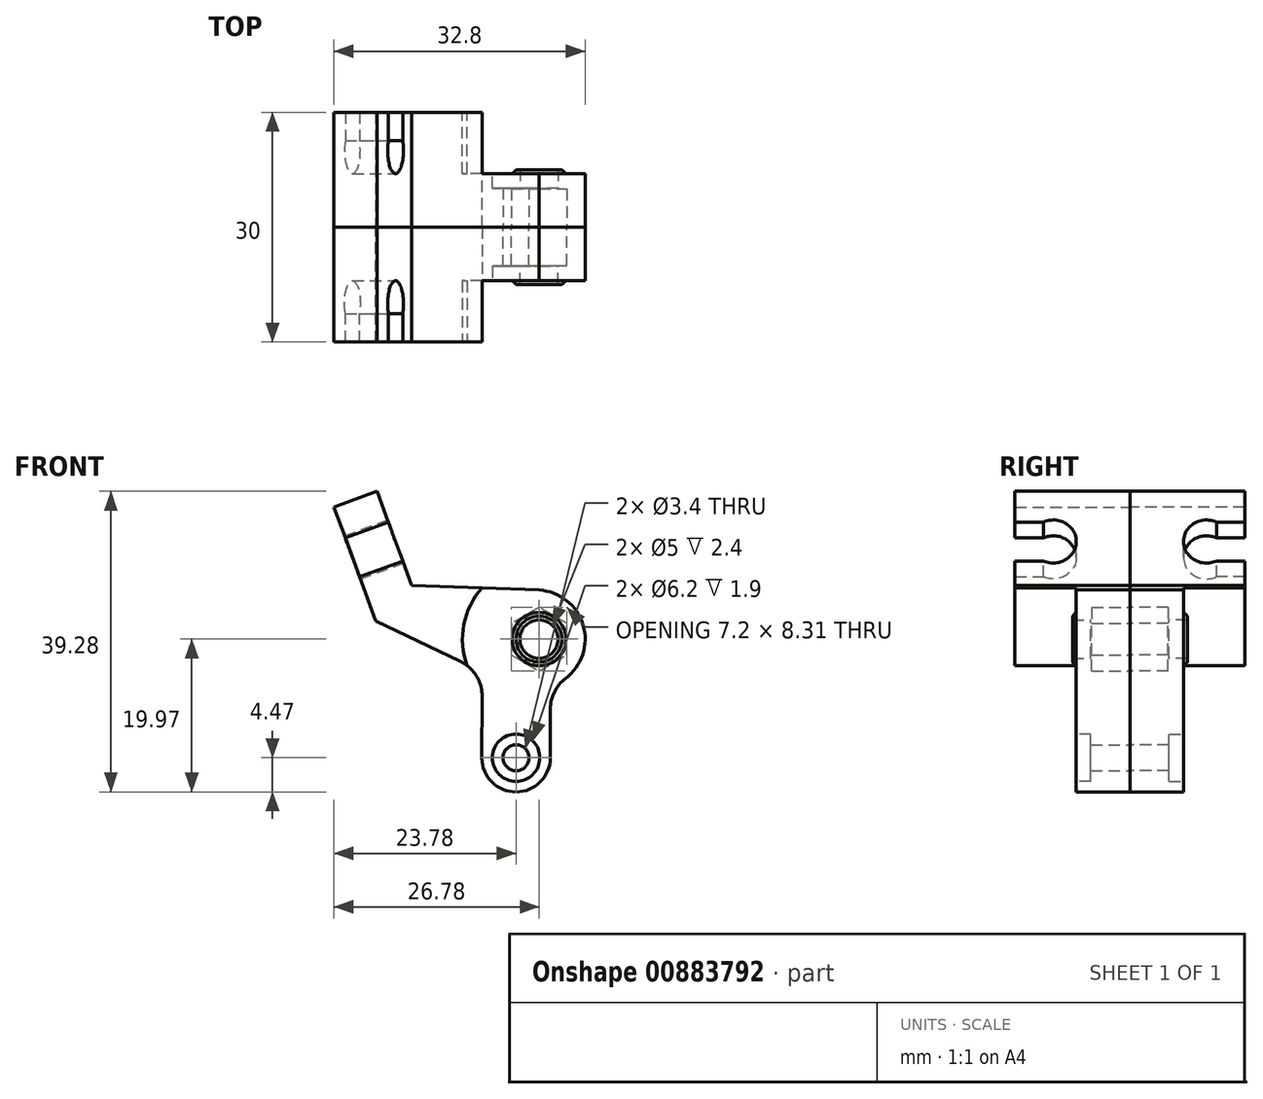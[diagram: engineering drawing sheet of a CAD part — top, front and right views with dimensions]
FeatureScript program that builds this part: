
annotation { "Feature Type Name" : "Feature", "Feature Type Description" : "" }
export const myFeature = defineFeature(function(context is Context, id is Id, definition is map)
    precondition{}
    {
        {
            var Q0;
            Q0=qCreatedBy(makeId("Front.planeOp"),FACE);
            var sketch = newSketch(context, id + "F0", { "sketchPlane" : qUnion([Q0])});
            skLineSegment(sketch, "E0", {"start": v(0, 0) * mm, "end": v(0, 3.63) * mm, "construction": true});
            skLineSegment(sketch, "E1", {"start": v(0, 0) * mm, "end": v(0, -20.28) * mm, "construction": true});
            skLineSegment(sketch, "E2", {"start": v(-4.5, 0) * mm, "end": v(4.5, 0) * mm, "construction": true});
            skCircle(sketch, "E3", {"center": v(0, 0) * mm, "radius": 3.5 * mm});
            skCircle(sketch, "E4", {"center": v(0, 0) * mm, "radius": 2.5 * mm});
            skCircle(sketch, "E5", {"center": v(0, 0) * mm, "radius": 10 * mm});
            skCircle(sketch, "E6", {"center": v(-3, -15.5) * mm, "radius": 1.7 * mm});
            skCircle(sketch, "E7", {"center": v(-3, -15.5) * mm, "radius": 3.1 * mm});
            skPoint(sketch, "E8.1", {"position": v(1.47, -15.5) * mm});
            skPoint(sketch, "E9.0", {"position": v(-9.43, -3.32) * mm});
            skPoint(sketch, "E9.3", {"position": v(-21.32, 2.4) * mm});
            skPoint(sketch, "E9.4", {"position": v(-26.78, 17.24) * mm});
            skPoint(sketch, "E9.5", {"position": v(-21.14, 19.31) * mm});
            skPoint(sketch, "E9.6", {"position": v(-16.64, 7.04) * mm});
            skCircle(sketch, "E10", {"center": v(0, 0) * mm, "radius": 4.5 * mm});
            skLineSegment(sketch, "E11", {"start": v(-7.47, -15.5) * mm, "end": v(-7.43, -4.29) * mm});
            skLineSegment(sketch, "E12", {"start": v(-21.32, 2.4) * mm, "end": v(-16.64, 7.04) * mm});
            skLineSegment(sketch, "E13", {"start": v(-16.64, 7.04) * mm, "end": v(0, 6.41) * mm});
            skLineSegment(sketch, "E14", {"start": v(1.5, -6.14) * mm, "end": v(1.47, -15.5) * mm});
            skLineSegment(sketch, "E15", {"start": v(-7.43, -4.29) * mm, "end": v(-21.32, 2.4) * mm});
            skArc(sketch, "E16", {"start": v(1.47, -15.5) * mm, "mid": v(-3, -19.97) * mm, "end": v(-7.47, -15.5) * mm});
            skArc(sketch, "E17", {"start": v(1.5, -6.14) * mm, "mid": v(5.96, 0.92) * mm, "end": v(-0.32, 6.42) * mm});
            skLineSegment(sketch, "E18", {"start": v(-21.32, 2.4) * mm, "end": v(-26.78, 17.24) * mm});
            skLineSegment(sketch, "E19", {"start": v(-26.78, 17.24) * mm, "end": v(-21.14, 19.31) * mm});
            skLineSegment(sketch, "E20", {"start": v(-21.14, 19.31) * mm, "end": v(-16.64, 7.04) * mm});
            skSolve(sketch);
        }
        {
            var Q0;
            Q0=makeQuery(id+"F0.imprint","IMPRINT",FACE,{"disambiguationData":[TD([[makeQuery(id+"F0.imprint","IMPRINT",EDGE,{"derivedFrom":sQuery(id+"F0.wireOp",EDGE,"E6")}),-1.0]])]});
            var Q1;
            Q1=makeQuery(id+"F0.imprint","IMPRINT",FACE,{"disambiguationData":[TD([[makeQuery(id+"F0.imprint","IMPRINT",EDGE,{"derivedFrom":sQuery(id+"F0.wireOp",EDGE,"E7")}),-1.0]])]});
            var Q2;
            Q2=makeQuery(id+"F0.imprint","IMPRINT",FACE,{"disambiguationData":[TD([[makeQuery(id+"F0.imprint","IMPRINT",EDGE,{"derivedFrom":sQuery(id+"F0.wireOp",EDGE,"E10")}),-1.0]])]});
            var Q3;
            {var subQ5=sQuery(id+"F0.wireOp",EDGE,"E12");Q3=makeQuery(id+"F0.imprint","IMPRINT",FACE,{"disambiguationData":[TD([[makeQuery(id+"F0.imprint","IMPRINT",EDGE,{"derivedFrom":subQ5}),-1.0]])]});}
            var Q4;
            Q4=makeQuery(id+"F0.imprint","IMPRINT",FACE,{"disambiguationData":[TD([[makeQuery(id+"F0.imprint","IMPRINT",EDGE,{"derivedFrom":sQuery(id+"F0.wireOp",EDGE,"E12")}),1.0]])]});
            var Q5;
            Q5=makeQuery(id+"F0.imprint","IMPRINT",FACE,{"disambiguationData":[TD([[makeQuery(id+"F0.imprint","IMPRINT",EDGE,{"derivedFrom":sQuery(id+"F0.wireOp",EDGE,"E3")}),1.0]])]});
            var Q6;
            Q6=makeQuery(id+"F0.imprint","IMPRINT",FACE,{"disambiguationData":[TD([[makeQuery(id+"F0.imprint","IMPRINT",EDGE,{"derivedFrom":sQuery(id+"F0.wireOp",EDGE,"E3")}),-1.0]])]});
            var Q7;
            Q7=makeQuery(id+"F0.imprint","IMPRINT",FACE,{"disambiguationData":[TD([[makeQuery(id+"F0.imprint","IMPRINT",EDGE,{"derivedFrom":sQuery(id+"F0.wireOp",EDGE,"E4")}),1.0]])]});
            extrude(context, id + "F1", {"entities" : qUnion([Q0, Q1, Q2, Q3, Q4, Q5, Q6, Q7]), "depth" : 15 * mm, "offsetDistance" : 25 * mm});
        }
        {
            var Q0;
            Q0=makeQuery(id+"F1.opExtrude","CAP_FACE",FACE,{"disambiguationData":[OSD([sQuery(id+"F0.wireOp",EDGE,"E4"),sQuery(id+"F0.wireOp",EDGE,"E6"),sQuery(id+"F0.wireOp",EDGE,"E11"),sQuery(id+"F0.wireOp",EDGE,"E13"),sQuery(id+"F0.wireOp",EDGE,"E14"),sQuery(id+"F0.wireOp",EDGE,"E15"),sQuery(id+"F0.wireOp",EDGE,"E16"),sQuery(id+"F0.wireOp",EDGE,"E17"),sQuery(id+"F0.wireOp",EDGE,"E18"),sQuery(id+"F0.wireOp",EDGE,"E19"),sQuery(id+"F0.wireOp",EDGE,"E20")])],"isStart":false});
            var sketch = newSketch(context, id + "F2", { "sketchPlane" : qUnion([Q0])});
            skCircle(sketch, "E21.0", {"center": v(0, 0) * mm, "radius": 10 * mm});
            skSolve(sketch);
        }
        {
            var Q0;
            {var subQ5=makeQuery(id+"F1.opExtrude","CAP_EDGE",EDGE,{"disambiguationData":[OSD([sQuery(id+"F0.wireOp",EDGE,"E17")])],"isStart":false});Q0=makeQuery(id+"F2.imprint","IMPRINT",FACE,{"disambiguationData":[TD([[makeQuery(id+"F2.imprint","IMPRINT",EDGE,{"derivedFrom":subQ5}),-1.0]])]});}
            var Q1;
            {var subQ7=makeQuery(id+"F1.opExtrude","CAP_EDGE",EDGE,{"disambiguationData":[OSD([sQuery(id+"F0.wireOp",EDGE,"E17")])],"isStart":false});Q1=makeQuery(id+"F2.imprint","IMPRINT",FACE,{"disambiguationData":[TD([[makeQuery(id+"F2.imprint","IMPRINT",EDGE,{"derivedFrom":subQ7}),1.0]])]});}
            var Q2;
            Q2=makeQuery(id+"F2.imprint","IMPRINT",FACE,{"disambiguationData":[TD([[makeQuery(id+"F2.imprint","IMPRINT",EDGE,{"derivedFrom":makeQuery(id+"F1.opExtrude","CAP_EDGE",EDGE,{"disambiguationData":[OSD([sQuery(id+"F0.wireOp",EDGE,"E6")])],"isStart":false})}),-1.0]])]});
            extrude(context, id + "F3", {"entities" : qUnion([Q0, Q1, Q2]), "operationType" : NewBodyOperationType.REMOVE, "oppositeDirection" : true, "depth" : 8 * mm, "offsetDistance" : 25 * mm});
        }
        {
            var Q0;
            Q0=makeQuery(id+"F1.opExtrude","SWEPT_EDGE",EDGE,{"disambiguationData":[OSD([sQuery(id+"F0.wireOp",EDGE,"E11"),sQuery(id+"F0.wireOp",EDGE,"E15")])]});
            var Q1;
            Q1=makeQuery(id+"F1.opExtrude","SWEPT_EDGE",EDGE,{"disambiguationData":[OSD([sQuery(id+"F0.wireOp",EDGE,"E14"),sQuery(id+"F0.wireOp",EDGE,"E17")])]});
            fillet(context, id + "F4", {"entities" : qUnion([Q0, Q1]), "radius" : 5 * mm, "tangentPropagation" : true, "allowEdgeOverflow" : false});
        }
        {
            var Q0;
            Q0=makeQuery(id+"F1.opExtrude","SWEPT_FACE",FACE,{"disambiguationData":[OSD([sQuery(id+"F0.wireOp",EDGE,"E20")])]});
            var sketch = newSketch(context, id + "F5", { "sketchPlane" : qUnion([Q0])});
            skLineSegment(sketch, "E22", {"start": v(-15, 21.12) * mm, "end": v(-7, 21.12) * mm, "construction": true});
            skPoint(sketch, "E23.0", {"position": v(-15, 25.42) * mm});
            skLineSegment(sketch, "E24", {"start": v(-15, 15.72) * mm, "end": v(-7, 15.72) * mm, "construction": true});
            skCircle(sketch, "E25", {"center": v(-10, 18.42) * mm, "radius": 3 * mm});
            skLineSegment(sketch, "E26", {"start": v(-15.9, 18.42) * mm, "end": v(-7, 18.42) * mm, "construction": true});
            skPoint(sketch, "E27", {"position": v(-11.45, 18.42) * mm});
            skLineSegment(sketch, "E28", {"start": v(-11.3, 15.72) * mm, "end": v(-15, 15.72) * mm});
            skLineSegment(sketch, "E29", {"start": v(-11.3, 21.12) * mm, "end": v(-15, 21.12) * mm});
            skSolve(sketch);
        }
        {
            var Q0;
            {var subQ0=sQuery(id+"F5.wireOp",EDGE,"E25");var subQ1=makeQuery(id+"F5.imprint","INTERSECT",VERTEX,{"derivedFrom":[subQ0,sQuery(id+"F5.wireOp",EDGE,"E28")]});Q0=makeQuery(id+"F5.imprint","IMPRINT",FACE,{"disambiguationData":[TD([[makeQuery(id+"F5.imprint","IMPRINT",EDGE,{"disambiguationData":[TD([[subQ1,1.0]])],"derivedFrom":subQ0}),1.0]])]});}
            var Q1;
            {var subQ0=sQuery(id+"F5.wireOp",EDGE,"E28");Q1=makeQuery(id+"F5.imprint","IMPRINT",FACE,{"disambiguationData":[TD([[makeQuery(id+"F5.imprint","IMPRINT",EDGE,{"derivedFrom":subQ0}),-1.0]])]});}
            extrude(context, id + "F6", {"entities" : qUnion([Q0, Q1]), "operationType" : NewBodyOperationType.REMOVE, "endBound" : BoundingType.THROUGH_ALL, "oppositeDirection" : true, "depth" : 25 * mm, "offsetDistance" : 25 * mm});
        }
        {
            var Q0;
            Q0=makeQuery(id+"F1.opExtrude","CAP_FACE",FACE,{"disambiguationData":[OSD([sQuery(id+"F0.wireOp",EDGE,"E6"),sQuery(id+"F0.wireOp",EDGE,"E11"),sQuery(id+"F0.wireOp",EDGE,"E13"),sQuery(id+"F0.wireOp",EDGE,"E14"),sQuery(id+"F0.wireOp",EDGE,"E15"),sQuery(id+"F0.wireOp",EDGE,"E16"),sQuery(id+"F0.wireOp",EDGE,"E17"),sQuery(id+"F0.wireOp",EDGE,"E18"),sQuery(id+"F0.wireOp",EDGE,"E19"),sQuery(id+"F0.wireOp",EDGE,"E20")])],"isStart":true});
            var sketch = newSketch(context, id + "F7", { "sketchPlane" : qUnion([Q0])});
            skCircle(sketch, "E30.cCircle", {"center": v(0, 0) * mm, "radius": 3.6 * mm, "construction": true});
            skLineSegment(sketch, "E30.0", {"start": v(-3.6, -2.08) * mm, "end": v(-3.6, 2.08) * mm});
            skLineSegment(sketch, "E30.1", {"start": v(-3.6, 2.08) * mm, "end": v(0, 4.16) * mm});
            skLineSegment(sketch, "E30.2", {"start": v(0, 4.16) * mm, "end": v(3.6, 2.08) * mm});
            skLineSegment(sketch, "E30.3", {"start": v(3.6, 2.08) * mm, "end": v(3.6, -2.08) * mm});
            skLineSegment(sketch, "E30.4", {"start": v(3.6, -2.08) * mm, "end": v(0, -4.16) * mm});
            skLineSegment(sketch, "E30.5", {"start": v(0, -4.16) * mm, "end": v(-3.6, -2.08) * mm});
            skPoint(sketch, "E30.0.midPoint", {"position": v(-3.6, 0) * mm});
            skSolve(sketch);
        }
        {
            var Q0;
            Q0=makeQuery(id+"F7.imprint","IMPRINT",FACE,{"disambiguationData":[TD([[makeQuery(id+"F7.imprint","IMPRINT",EDGE,{"derivedFrom":sQuery(id+"F7.wireOp",EDGE,"E30.0")}),-1.0]])]});
            extrude(context, id + "F8", {"entities" : qUnion([Q0]), "operationType" : NewBodyOperationType.REMOVE, "oppositeDirection" : true, "depth" : 5 * mm, "offsetDistance" : 25 * mm});
        }
        {
            var Q0;
            Q0=makeQuery(id+"F3.boolean.opBoolean","COPY",FACE,{"derivedFrom":makeQuery(id+"F3.opExtrude","CAP_FACE",FACE,{"disambiguationData":[OSD([sQuery(id+"F0.wireOp",EDGE,"E4"),sQuery(id+"F0.wireOp",EDGE,"E6"),sQuery(id+"F0.wireOp",EDGE,"E11"),sQuery(id+"F0.wireOp",EDGE,"E14"),sQuery(id+"F0.wireOp",EDGE,"E15"),sQuery(id+"F0.wireOp",EDGE,"E16"),sQuery(id+"F2.wireOp",EDGE,"E21.0")])],"isStart":false})});
            var sketch = newSketch(context, id + "F9", { "sketchPlane" : qUnion([Q0])});
            skCircle(sketch, "E31.1", {"center": v(0, 0) * mm, "radius": 3.5 * mm});
            skCircle(sketch, "E32.0", {"center": v(-3, -15.5) * mm, "radius": 3.1 * mm});
            skCircle(sketch, "E33.0", {"center": v(0, 0) * mm, "radius": 2.5 * mm});
            skSolve(sketch);
        }
        {
            var Q0;
            Q0=makeQuery(id+"F9.imprint","IMPRINT",FACE,{"disambiguationData":[TD([[makeQuery(id+"F9.imprint","IMPRINT",EDGE,{"derivedFrom":sQuery(id+"F9.wireOp",EDGE,"E31.1")}),1.0]])]});
            extrude(context, id + "F10", {"entities" : qUnion([Q0]), "operationType" : NewBodyOperationType.ADD, "depth" : 0.5 * mm, "offsetDistance" : 25 * mm});
        }
        {
            var Q0;
            Q0=makeQuery(id+"F9.imprint","IMPRINT",FACE,{"disambiguationData":[TD([[makeQuery(id+"F9.imprint","IMPRINT",EDGE,{"derivedFrom":sQuery(id+"F9.wireOp",EDGE,"E32.0")}),1.0]])]});
            var Q1;
            Q1=makeQuery(id+"F9.imprint","IMPRINT",FACE,{"disambiguationData":[TD([[makeQuery(id+"F9.imprint","IMPRINT",EDGE,{"derivedFrom":sQuery(id+"F9.wireOp",EDGE,"E33.0")}),1.0]])]});
            extrude(context, id + "F11", {"entities" : qUnion([Q0, Q1]), "operationType" : NewBodyOperationType.REMOVE, "oppositeDirection" : true, "depth" : 1.9 * mm, "offsetDistance" : 25 * mm});
        }
        {
            var Q0;
            Q0=makeQuery(id+"F10.opExtrude","CAP_EDGE",EDGE,{"disambiguationData":[OSD([sQuery(id+"F9.wireOp",EDGE,"E31.1")])],"isStart":false});
            chamfer(context, id + "F12", {"entities" : qUnion([Q0]), "width" : 0.5 * mm, "tangentPropagation" : true});
        }
        {
            var Q0;
            Q0=makeQuery(id+"F1.opExtrude","SWEPT_BODY",BODY,{"disambiguationData":[OSD([sQuery(id+"F0.wireOp",EDGE,"E6"),sQuery(id+"F0.wireOp",EDGE,"E11"),sQuery(id+"F0.wireOp",EDGE,"E13"),sQuery(id+"F0.wireOp",EDGE,"E14"),sQuery(id+"F0.wireOp",EDGE,"E15"),sQuery(id+"F0.wireOp",EDGE,"E16"),sQuery(id+"F0.wireOp",EDGE,"E17"),sQuery(id+"F0.wireOp",EDGE,"E18"),sQuery(id+"F0.wireOp",EDGE,"E19"),sQuery(id+"F0.wireOp",EDGE,"E20")])]});
            var Q1;
            Q1=qCreatedBy(makeId("Front.planeOp"),FACE);
            mirror(context, id + "F13", {"entities" : qUnion([Q0]), "mirrorPlane" : qUnion([Q1])});
        }
    });
